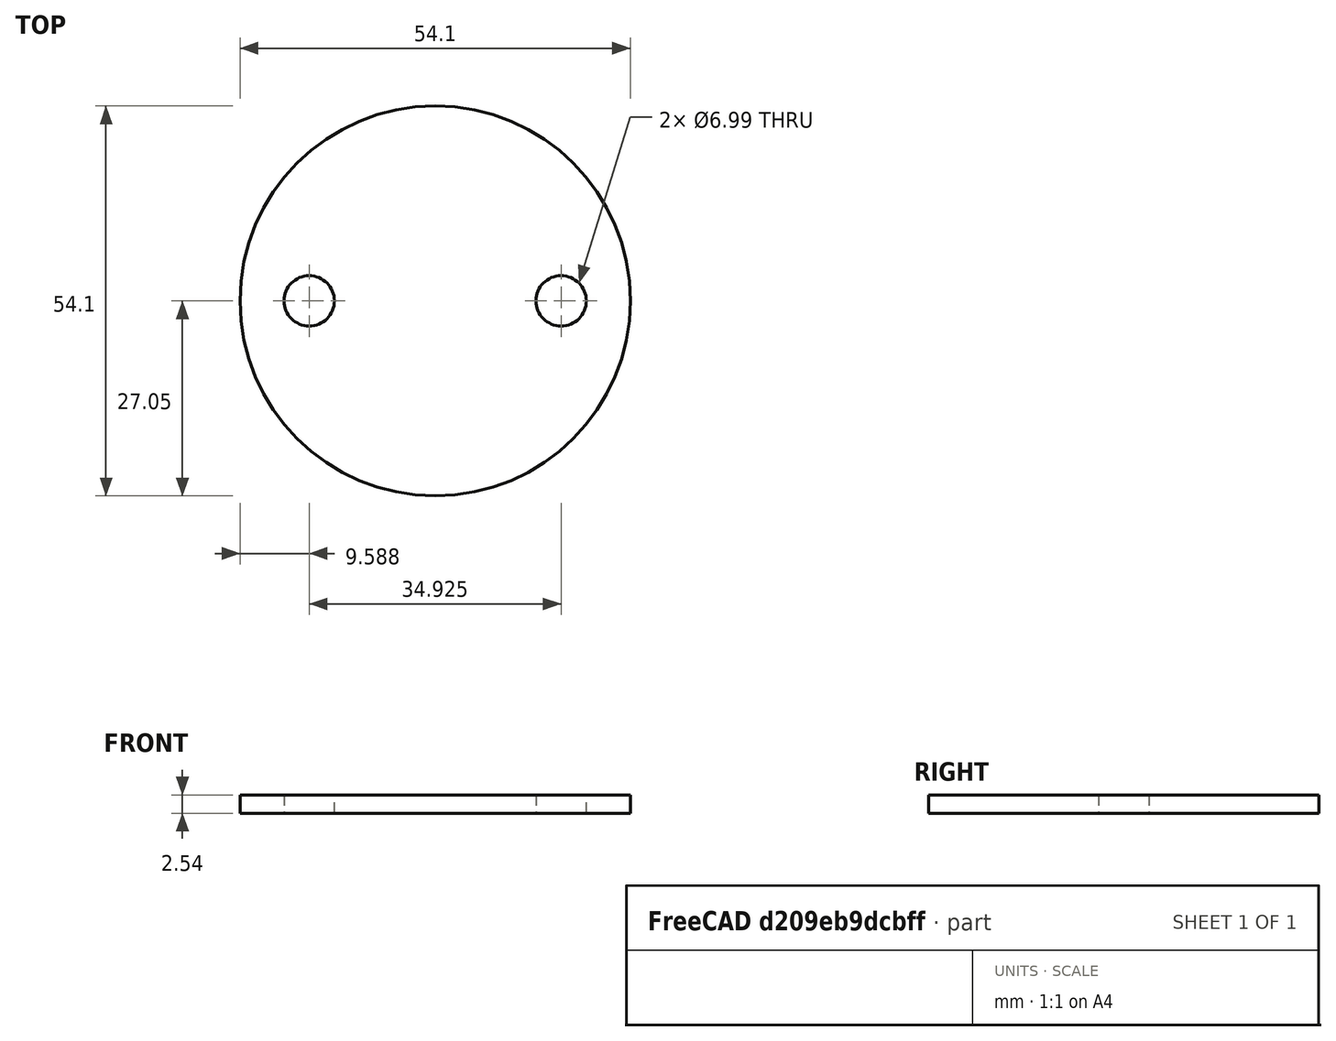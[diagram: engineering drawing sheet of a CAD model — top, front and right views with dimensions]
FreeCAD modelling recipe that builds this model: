
FCSTD DOCUMENT  (FreeCAD 0.19R24291 (Git))
Label: david base
License: Creative Commons Attribution-ShareAlike
LicenseURL: http://creativecommons.org/licenses/by-sa/4.0/
objects: Sketcher::SketchObject×1, PartDesign::Pad×1, PartDesign::Body×1
note: 4 computed .brp shape members not serialized (recipe doc carries the construction recipe); baked Part::Feature solids carry a one-line shape summary decoded from their .brp

FEATURE [Sketcher::SketchObject] Sketch
  FullyConstrained = true
  MapMode = 5
  Support = -> [XY_Plane]
  sketch-geometry (6):
    g0: Circle CenterX=0 CenterY=0 CenterZ=0 NormalX=0 NormalY=0 NormalZ=1 AngleXU=0 Radius=27.051
    g1: Circle CenterX=-17.4625 CenterY=0 CenterZ=0 NormalX=0 NormalY=0 NormalZ=1 AngleXU=0 Radius=3.4925
    g2: Circle CenterX=17.4625 CenterY=0 CenterZ=0 NormalX=0 NormalY=0 NormalZ=1 AngleXU=0 Radius=3.4925
    g3: LineSegment StartX=-27.051 StartY=0 StartZ=0 EndX=-20.955 EndY=0 EndZ=0
    g4: LineSegment StartX=20.955 StartY=0 StartZ=0 EndX=27.051 EndY=0 EndZ=0
    g5: LineSegment StartX=-13.97 StartY=0 StartZ=0 EndX=13.97 EndY=0 EndZ=0
  constraints (17):
    c: Coincident(g0,g-1)
    c: PointOnObject(g1,g-1)
    c: PointOnObject(g2,g-1)
    c: Equal(g1,g2)
    c: Diameter(g0) = 54.102
    c: PointOnObject(g3,g0)
    c: PointOnObject(g3,g1)
    c: PointOnObject(g4,g2)
    c: PointOnObject(g4,g0)
    c: Tangent(g4,g-1)
    c: Tangent(g3,g-1)
    c: Equal(g4,g3)
    c: PointOnObject(g5,g1)
    c: PointOnObject(g5,g2)
    c: Tangent(g-1,g5)
    c: DistanceX(g5,g5) = 27.94
    c: DistanceX(g3,g4) = 41.91
FEATURE [PartDesign::Pad] Pad
  Direction = (1,1,1)
  Length = 2.54
  Length2 = 99.9998
  Profile = -> Sketch
  Type = 0
FEATURE [PartDesign::Body] Body
  Group = -> [Sketch,Pad]
  Origin = -> Origin
  Tip = -> Pad
